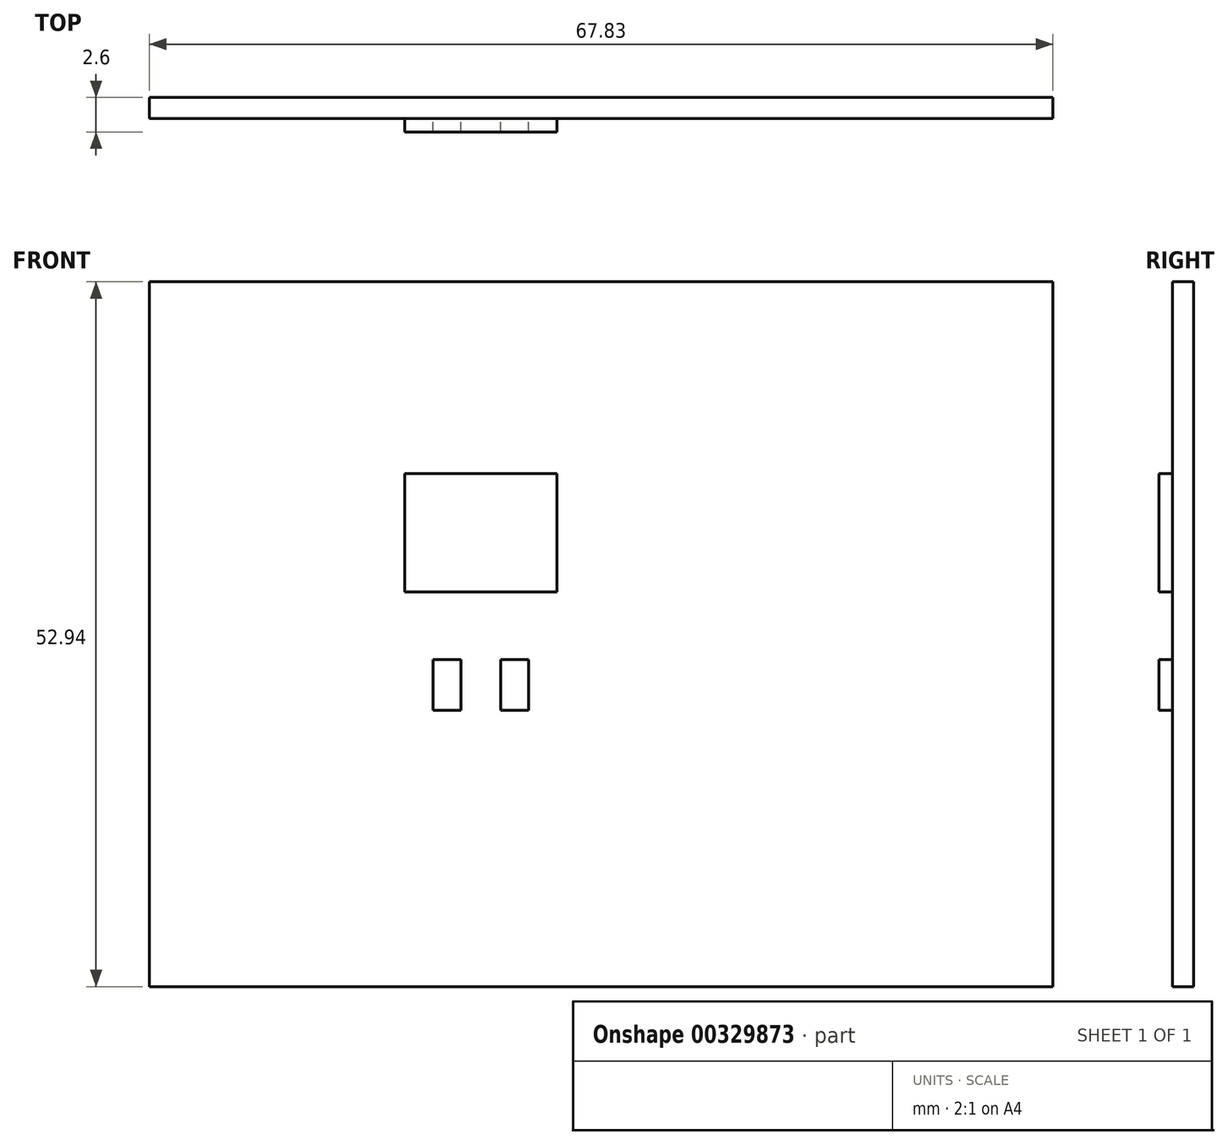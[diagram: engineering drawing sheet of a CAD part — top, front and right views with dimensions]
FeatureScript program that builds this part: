
annotation { "Feature Type Name" : "Feature", "Feature Type Description" : "" }
export const myFeature = defineFeature(function(context is Context, id is Id, definition is map)
    precondition{}
    {
        {
            var Q0;
            Q0=qCreatedBy(makeId("Front.planeOp"),FACE);
            var sketch = newSketch(context, id + "F0", { "sketchPlane" : qUnion([Q0])});
            skLineSegment(sketch, "E0.bottom", {"start": v(-24.89, 23.56) * mm, "end": v(42.94, 23.56) * mm});
            skLineSegment(sketch, "E0.top", {"start": v(-24.89, -29.38) * mm, "end": v(42.94, -29.38) * mm});
            skLineSegment(sketch, "E0.left", {"start": v(-24.89, 23.56) * mm, "end": v(-24.89, -29.38) * mm});
            skLineSegment(sketch, "E0.right", {"start": v(42.94, 23.56) * mm, "end": v(42.94, -29.38) * mm});
            skSolve(sketch);
        }
        {
            var Q0;
            Q0 = qSketchRegion(id + "F0", true);
            extrude(context, id + "F1", {"entities" : qUnion([Q0]), "oppositeDirection" : true, "depth" : 1.6 * mm, "offsetDistance" : 25 * mm});
        }
        {
            var Q0;
            Q0=qCreatedBy(makeId("Front.planeOp"),FACE);
            var sketch = newSketch(context, id + "F2", { "sketchPlane" : qUnion([Q0])});
            skLineSegment(sketch, "E1.bottom", {"start": v(-3.58, -8.62) * mm, "end": v(-1.5, -8.62) * mm});
            skLineSegment(sketch, "E1.top", {"start": v(-3.58, -4.81) * mm, "end": v(-1.5, -4.81) * mm});
            skLineSegment(sketch, "E1.left", {"start": v(-3.58, -8.62) * mm, "end": v(-3.58, -4.81) * mm});
            skLineSegment(sketch, "E1.right", {"start": v(-1.5, -8.62) * mm, "end": v(-1.5, -4.81) * mm});
            skLineSegment(sketch, "E2.bottom", {"start": v(-5.72, 0.27) * mm, "end": v(5.71, 0.27) * mm});
            skLineSegment(sketch, "E2.top", {"start": v(-5.71, 9.16) * mm, "end": v(5.71, 9.16) * mm});
            skLineSegment(sketch, "E2.left", {"start": v(-5.72, 0.27) * mm, "end": v(-5.71, 9.16) * mm});
            skLineSegment(sketch, "E2.right", {"start": v(5.71, 0.27) * mm, "end": v(5.71, 9.16) * mm});
            skLineSegment(sketch, "E3", {"start": v(0, 0.27) * mm, "end": v(0, 0) * mm, "construction": true});
            skLineSegment(sketch, "E4", {"start": v(-5.72, 4.71) * mm, "end": v(5.71, 4.71) * mm, "construction": true});
            skLineSegment(sketch, "E5", {"start": v(0, 4.72) * mm, "end": v(0, 0.27) * mm, "construction": true});
            skLineSegment(sketch, "E6", {"start": v(-3.58, -6.72) * mm, "end": v(-2.54, -6.72) * mm, "construction": true});
            skPoint(sketch, "E6.endSnap0", {"position": v(-2.54, -4.81) * mm});
            skLineSegment(sketch, "E7.MirrorCS", {"start": v(1.5, -8.62) * mm, "end": v(1.5, -4.81) * mm});
            skLineSegment(sketch, "E8.MirrorCS", {"start": v(3.58, -4.8) * mm, "end": v(1.5, -4.8) * mm});
            skLineSegment(sketch, "E9.MirrorCS", {"start": v(3.58, -8.62) * mm, "end": v(3.58, -4.81) * mm});
            skLineSegment(sketch, "E10.MirrorCS", {"start": v(3.58, -8.62) * mm, "end": v(1.5, -8.62) * mm});
            skSolve(sketch);
        }
        {
            var Q0;
            Q0 = qSketchRegion(id + "F2", true);
            extrude(context, id + "F3", {"entities" : qUnion([Q0]), "depth" : 1 * mm, "offsetDistance" : 25 * mm});
        }
    });
